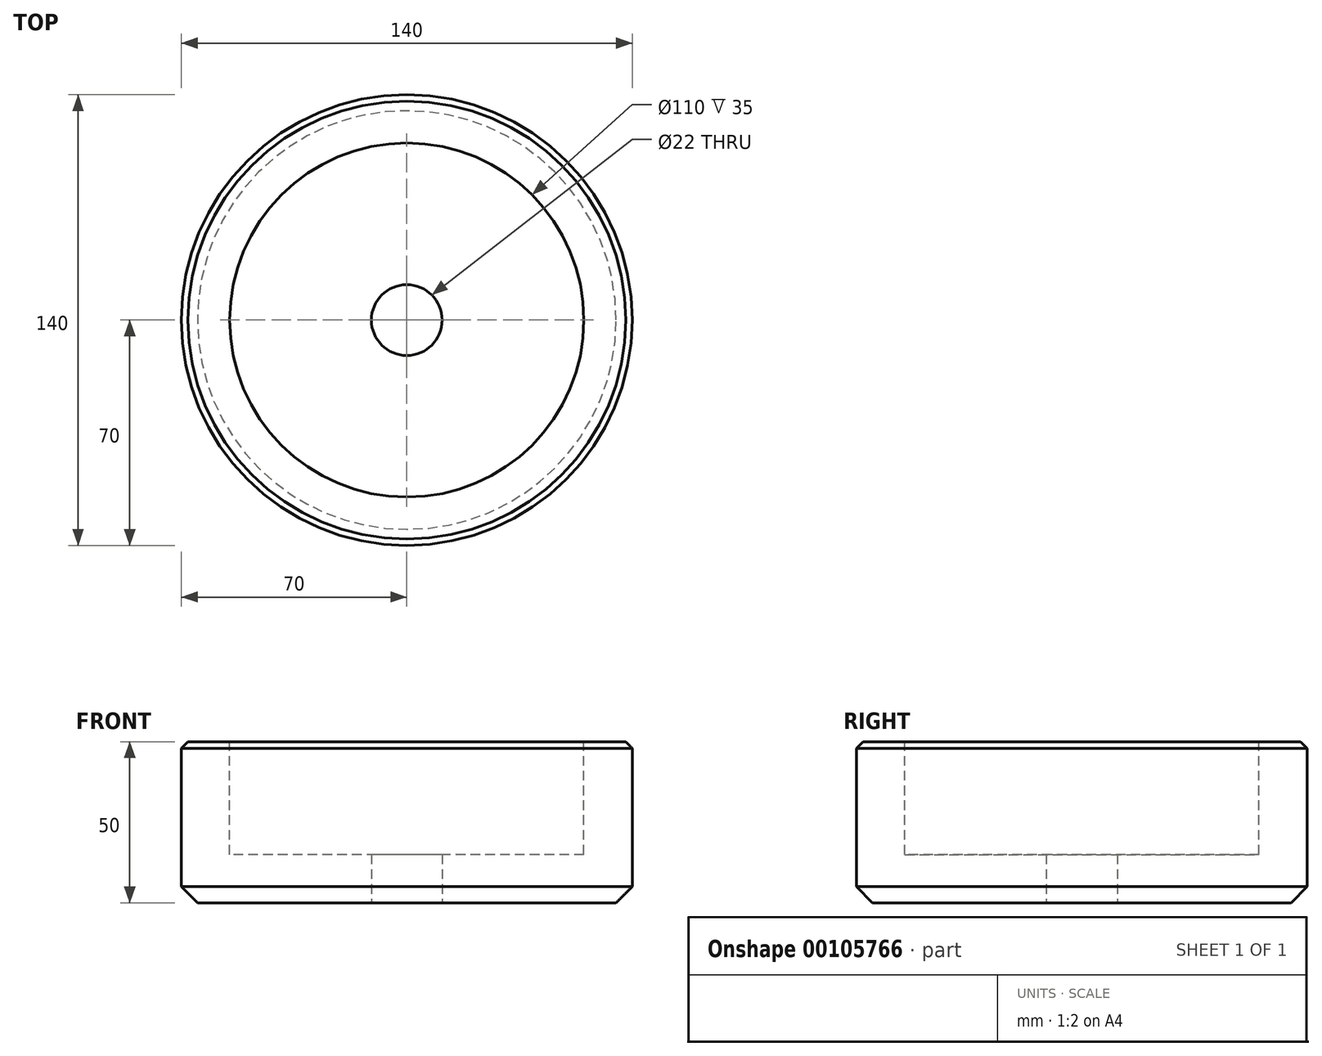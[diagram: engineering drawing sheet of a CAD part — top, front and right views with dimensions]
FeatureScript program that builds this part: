
annotation { "Feature Type Name" : "Feature", "Feature Type Description" : "" }
export const myFeature = defineFeature(function(context is Context, id is Id, definition is map)
    precondition{}
    {
        {
            var Q0;
            Q0=qCreatedBy(makeId("Top.planeOp"),FACE);
            var sketch = newSketch(context, id + "F0", { "sketchPlane" : qUnion([Q0])});
            skCircle(sketch, "E0", {"center": v(0, 0) * mm, "radius": 70 * mm});
            skSolve(sketch);
        }
        {
            var Q0;
            Q0=makeQuery(id+"F0.imprint","IMPRINT",FACE,{"disambiguationData":[TD([[makeQuery(id+"F0.imprint","IMPRINT",EDGE,{"derivedFrom":sQuery(id+"F0.wireOp",EDGE,"E0")}),1.0]])]});
            extrude(context, id + "F1", {"entities" : qUnion([Q0]), "depth" : 50 * mm});
        }
        {
            var Q0;
            Q0=makeQuery(id+"F1.opExtrude","CAP_FACE",FACE,{"disambiguationData":[OSD([sQuery(id+"F0.wireOp",EDGE,"E0")])],"isStart":false});
            var sketch = newSketch(context, id + "F2", { "sketchPlane" : qUnion([Q0])});
            skCircle(sketch, "E1", {"center": v(0, 0) * mm, "radius": 55 * mm});
            skSolve(sketch);
        }
        {
            var Q0;
            Q0=makeQuery(id+"F2.imprint","IMPRINT",FACE,{"disambiguationData":[TD([[makeQuery(id+"F2.imprint","IMPRINT",EDGE,{"derivedFrom":sQuery(id+"F2.wireOp",EDGE,"E1")}),1.0]])]});
            extrude(context, id + "F3", {"entities" : qUnion([Q0]), "operationType" : NewBodyOperationType.REMOVE, "oppositeDirection" : true, "depth" : 35 * mm});
        }
        {
            var Q0;
            Q0=makeQuery(id+"F1.opExtrude","CAP_EDGE",EDGE,{"disambiguationData":[OSD([sQuery(id+"F0.wireOp",EDGE,"E0")])],"isStart":true});
            chamfer(context, id + "F4", {"entities" : qUnion([Q0]), "width" : 5 * mm, "tangentPropagation" : true});
        }
        {
            var Q0;
            Q0=makeQuery(id+"F1.opExtrude","CAP_EDGE",EDGE,{"disambiguationData":[OSD([sQuery(id+"F0.wireOp",EDGE,"E0")])],"isStart":false});
            var Q1;
            Q1=makeQuery(id+"F3.boolean.opBoolean","COPY",EDGE,{"derivedFrom":makeQuery(id+"F3.opExtrude","CAP_EDGE",EDGE,{"disambiguationData":[OSD([sQuery(id+"F2.wireOp",EDGE,"E1")])],"isStart":true})});
            chamfer(context, id + "F5", {"entities" : qUnion([Q0, Q1]), "width" : 2 * mm, "tangentPropagation" : true});
        }
        {
            var Q0;
            Q0=makeQuery(id+"F1.opExtrude","CAP_FACE",FACE,{"disambiguationData":[OSD([sQuery(id+"F0.wireOp",EDGE,"E0")])],"isStart":true});
            var sketch = newSketch(context, id + "F6", { "sketchPlane" : qUnion([Q0])});
            skPoint(sketch, "E2", {"position": v(0, 0) * mm});
            skSolve(sketch);
        }
        {
            var Q0;
            Q0=sQuery(id+"F6.wireOp",VERTEX,"E2");
            var Q1;
            Q1=makeQuery(id+"F1.opExtrude","SWEPT_BODY",BODY,{"disambiguationData":[OSD([sQuery(id+"F0.wireOp",EDGE,"E0")])]});
            hole(context, id + "F7", {"style" : HoleStyle.SIMPLE, "endStyle" : HoleEndStyle.BLIND, "standardTappedOrClearance" : lookupTablePath({ "standard" : "ISO", "fit" : "Normal", "size" : "M20", "type" : "Clearance" }), "standardBlindInLast" : lookupTablePath({ "fit" : "Standard", "standard" : "ISO", "size" : "M20", "type" : "Clearance" }), "holeDiameter" : 22 * mm, "holeDepth" : 30 * mm, "locations" : qUnion([Q0]), "scope" : qUnion([Q1])});
        }
    });
